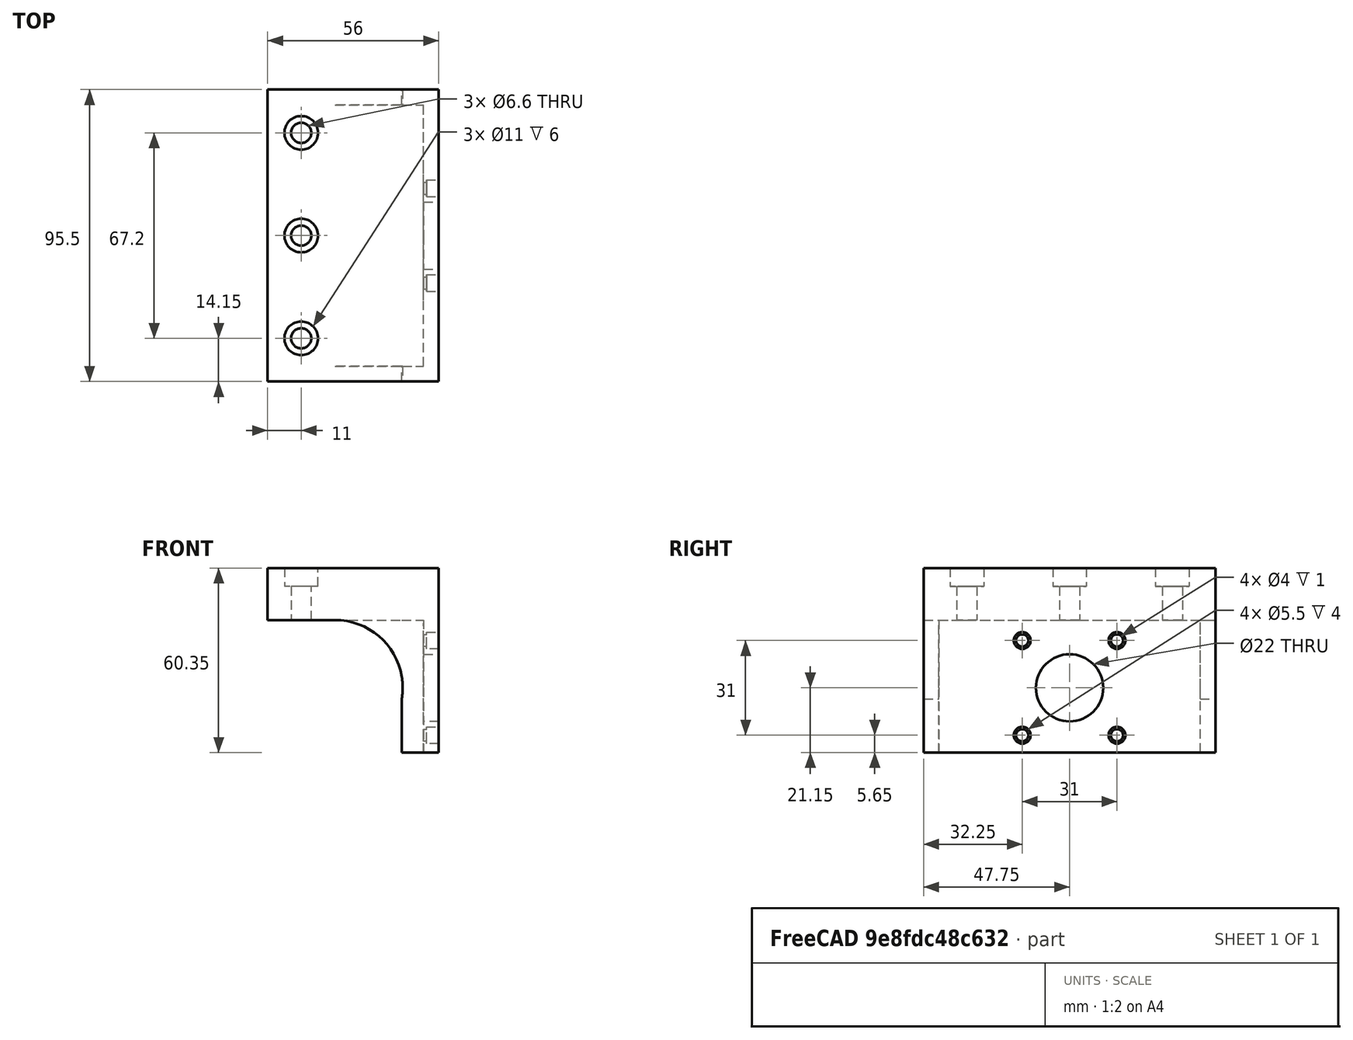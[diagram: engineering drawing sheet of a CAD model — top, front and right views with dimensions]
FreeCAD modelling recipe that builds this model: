
FCSTD DOCUMENT  (FreeCAD 1.0R1.0.0)
Label: CrossTableMount01
License: All rights reserved
LicenseURL: http://en.wikipedia.org/wiki/All_rights_reserved
objects: Part::Cylinder×8, Part::MultiFuse×8, Part::Box×7, Part::Cut×4, Spreadsheet::Sheet×1, Part::Feature×1, Part::Compound×1
note: 29 computed .brp shape members not serialized (recipe doc carries the construction recipe); baked Part::Feature solids carry a one-line shape summary decoded from their .brp

FEATURE [Spreadsheet::Sheet] Spreadsheet
  cells = A2='Slot spacing; B2(slot_spacing)==42.2 - 8.6; E2='Upper thickness; F2(upper_total_thickness)==clamp_screwlen - slot_depth + clamp_headheight; A3='Slot depth; B3(slot_depth)=9; E3='Screw thread thickness; F3(screwhole_len)==clamp_screwlen - slot_depth; A4='Clamp screw through hole; B4(clamp_through)=6.6; C4='M6 medium through hole; A5='Clamp screw length; B5(clamp_screwlen)=20; C5='without head as usual; A6='Clamp screw head diameter; B6(clamp_headdia)=11; C6='Real diameter is 10, want to make sure it fits; A7='Clamp screw head height; B7(clamp_headheight)=6; C7='Real height is 6, want to sink; A8='Tolerance; B8(tolerance)=0.2; A9='Total width; B9(total_width)=95.5; A10='Motor offset horizontal; B10(motor_off_h)=34; A11='Motor offset vertical; B11(motor_off_v)==40 - 18.6 / 2 - 8.5
FEATURE [Part::Box] Box  label="Cube"
  AttacherType = Attacher::AttachEngine3D
  Height = 17
  Length = 56
  Placement = pos=(0,-47.75,0) rot=(0,0,1;0rad)
  Width = 95.5
  expr: .Placement.Base.y = -Spreadsheet.total_width / 2
  expr: Height = <<Spreadsheet>>.upper_total_thickness
  expr: Length = Spreadsheet.clamp_headdia * 2 + Spreadsheet.motor_off_h
  expr: Width = Spreadsheet.total_width
FEATURE [Part::Cylinder] Cylinder
  Angle = 360
  AttacherType = Attacher::AttachEngine3D
  FirstAngle = 0
  Height = 17
  Radius = 3.3
  SecondAngle = 0
  expr: Height = Spreadsheet.upper_total_thickness
  expr: Radius = Spreadsheet.clamp_through / 2
FEATURE [Part::Cylinder] Cylinder001
  Angle = 360
  AttacherType = Attacher::AttachEngine3D
  FirstAngle = 0
  Height = 6
  Placement = pos=(0,0,11) rot=(0,0,1;0rad)
  Radius = 5.5
  SecondAngle = 0
  expr: .Placement.Base.z = Spreadsheet.screwhole_len
  expr: Height = Spreadsheet.clamp_headheight
  expr: Radius = Spreadsheet.clamp_headdia / 2
FEATURE [Part::MultiFuse] Fusion
  Placement = pos=(11,0,0) rot=(0,0,1;0rad)
  Shapes = -> [Cylinder,Cylinder001]
  expr: .Placement.Base.x = Spreadsheet.clamp_headdia
FEATURE [Part::Cylinder] Cylinder002
  Angle = 360
  AttacherType = Attacher::AttachEngine3D
  FirstAngle = 0
  Height = 17
  Radius = 3.3
  SecondAngle = 0
  expr: Height = Spreadsheet.upper_total_thickness
  expr: Radius = Spreadsheet.clamp_through / 2
FEATURE [Part::Cylinder] Cylinder003
  Angle = 360
  AttacherType = Attacher::AttachEngine3D
  FirstAngle = 0
  Height = 6
  Placement = pos=(0,0,11) rot=(0,0,1;0rad)
  Radius = 5.5
  SecondAngle = 0
  expr: .Placement.Base.z = Spreadsheet.screwhole_len
  expr: Height = Spreadsheet.clamp_headheight
  expr: Radius = Spreadsheet.clamp_headdia / 2
FEATURE [Part::MultiFuse] Fusion001
  Placement = pos=(11,33.6,0) rot=(0,0,1;0rad)
  Shapes = -> [Cylinder002,Cylinder003]
  expr: .Placement.Base.x = Spreadsheet.clamp_headdia
  expr: .Placement.Base.y = Spreadsheet.slot_spacing
FEATURE [Part::Cylinder] Cylinder004
  Angle = 360
  AttacherType = Attacher::AttachEngine3D
  FirstAngle = 0
  Height = 17
  Radius = 3.3
  SecondAngle = 0
  expr: Height = Spreadsheet.upper_total_thickness
  expr: Radius = Spreadsheet.clamp_through / 2
FEATURE [Part::Cylinder] Cylinder005
  Angle = 360
  AttacherType = Attacher::AttachEngine3D
  FirstAngle = 0
  Height = 6
  Placement = pos=(0,0,11) rot=(0,0,1;0rad)
  Radius = 5.5
  SecondAngle = 0
  expr: .Placement.Base.z = Spreadsheet.screwhole_len
  expr: Height = Spreadsheet.clamp_headheight
  expr: Radius = Spreadsheet.clamp_headdia / 2
FEATURE [Part::MultiFuse] Fusion002
  Placement = pos=(11,-33.6,0) rot=(0,0,1;0rad)
  Shapes = -> [Cylinder004,Cylinder005]
  expr: .Placement.Base.x = Spreadsheet.clamp_headdia
  expr: .Placement.Base.y = -Spreadsheet.slot_spacing
FEATURE [Part::MultiFuse] Fusion003
  Shapes = -> [Fusion,Fusion001,Fusion002]
FEATURE [Part::Cut] Cut
  Base = -> Box
  Tool = -> Fusion003
FEATURE [Part::Feature] Cut003_solid  label="MountplateTemplate"
  Placement = pos=(0,0,0) rot=(0,1,0;1.5708rad)
  shape: bbox 5 x 42.3 x 42.3 mm, 19 faces (baked)
  expr: .Placement.Base.z = 0
FEATURE [Part::Box] Box001  label="Cube001"
  AttacherType = Attacher::AttachEngine3D
  Height = 60.35
  Length = 5
  Placement = pos=(51,-47.75,-43.35) rot=(0,0,1;0rad)
  Width = 95.5
  expr: .Placement.Base.x = Spreadsheet.motor_off_h - 5 + Spreadsheet.clamp_headdia * 2
  expr: .Placement.Base.y = -Spreadsheet.total_width / 2
  expr: .Placement.Base.z = -(42.3 / 2 + Spreadsheet.motor_off_v)
  expr: Height = 42.3 / 2 + Spreadsheet.motor_off_v + Spreadsheet.upper_total_thickness
  expr: Width = Spreadsheet.total_width
FEATURE [Part::Compound] Compound
  Links = -> [Cut003_solid]
  Placement = pos=(51,0,-22.2) rot=(0,0,1;3.14159rad)
  expr: .Placement.Base.x = Spreadsheet.motor_off_h + Spreadsheet.clamp_headdia * 2 - 5
  expr: .Placement.Base.z = -Spreadsheet.motor_off_v
FEATURE [Part::Box] Box002  label="Cube002"
  AttacherType = Attacher::AttachEngine3D
  Height = 42.3
  Length = 5
  Placement = pos=(51,-21.15,-43.35) rot=(0,0,1;0rad)
  Width = 42.3
  expr: .Placement.Base.x = Spreadsheet.motor_off_h - 5 + Spreadsheet.clamp_headdia * 2
  expr: .Placement.Base.y = -42.3 / 2
  expr: .Placement.Base.z = -Spreadsheet.motor_off_v - 42.3 / 2
FEATURE [Part::Cut] Cut001
  Base = -> Box001
  Tool = -> Box002
FEATURE [Part::MultiFuse] Fusion004
  Shapes = -> [Cut001,Compound]
FEATURE [Part::Box] Box003  label="Cube003"
  AttacherType = Attacher::AttachEngine3D
  Height = 22.2
  Length = 34
  Placement = pos=(22,0,-22.2) rot=(0,0,1;0rad)
  Width = 5
  expr: .Placement.Base.x = Spreadsheet.clamp_headdia * 2
  expr: .Placement.Base.z = -Spreadsheet.motor_off_v
  expr: Height = Spreadsheet.motor_off_v
  expr: Length = Spreadsheet.motor_off_h
FEATURE [Part::Cylinder] Cylinder006
  Angle = 360
  AttacherType = Attacher::AttachEngine3D
  FirstAngle = 0
  Height = 5
  Placement = pos=(22,5,-22.2) rot=(1,0,0;1.5708rad)
  Radius = 22.2
  SecondAngle = 0
  expr: .Placement.Base.x = 2 * Spreadsheet.clamp_headdia
  expr: .Placement.Base.z = -Spreadsheet.motor_off_v
  expr: Radius = Spreadsheet.motor_off_v
FEATURE [Part::Box] Box004  label="Cube004"
  AttacherType = Attacher::AttachEngine3D
  Height = 43.35
  Length = 11.1
  Placement = pos=(43.9,0,-43.35) rot=(0,0,1;0rad)
  Width = 5
  expr: .Placement.Base.x = 2 * Spreadsheet.clamp_headdia + Spreadsheet.motor_off_h - (Spreadsheet.motor_off_h - (Spreadsheet.motor_off_h - Spreadsheet.motor_off_v / 2)) - 1
  expr: .Placement.Base.z = -(Spreadsheet.motor_off_v + 42.3 / 2)
  expr: Height = Spreadsheet.motor_off_v + 42.3 / 2
  expr: Length = Spreadsheet.motor_off_h - (Spreadsheet.motor_off_h - Spreadsheet.motor_off_v / 2)
FEATURE [Part::MultiFuse] Fusion005
  Shapes = -> [Box003,Box004]
FEATURE [Part::Cut] Cut002
  Base = -> Fusion005
  Placement = pos=(0,42.75,0) rot=(0,0,1;0rad)
  Tool = -> Cylinder006
  expr: .Placement.Base.y = Spreadsheet.total_width / 2 - 5
FEATURE [Part::Box] Box005  label="Cube005"
  AttacherType = Attacher::AttachEngine3D
  Height = 22.2
  Length = 34
  Placement = pos=(22,0,-22.2) rot=(0,0,1;0rad)
  Width = 5
  expr: .Placement.Base.x = Spreadsheet.clamp_headdia * 2
  expr: .Placement.Base.z = -Spreadsheet.motor_off_v
  expr: Height = Spreadsheet.motor_off_v
  expr: Length = Spreadsheet.motor_off_h
FEATURE [Part::Box] Box006  label="Cube006"
  AttacherType = Attacher::AttachEngine3D
  Height = 43.35
  Length = 11.1
  Placement = pos=(43.9,0,-43.35) rot=(0,0,1;0rad)
  Width = 5
  expr: .Placement.Base.x = 2 * Spreadsheet.clamp_headdia + Spreadsheet.motor_off_h - (Spreadsheet.motor_off_h - (Spreadsheet.motor_off_h - Spreadsheet.motor_off_v / 2)) - 1
  expr: .Placement.Base.z = -(Spreadsheet.motor_off_v + 42.3 / 2)
  expr: Height = Spreadsheet.motor_off_v + 42.3 / 2
  expr: Length = Spreadsheet.motor_off_h - (Spreadsheet.motor_off_h - Spreadsheet.motor_off_v / 2)
FEATURE [Part::Cylinder] Cylinder007
  Angle = 360
  AttacherType = Attacher::AttachEngine3D
  FirstAngle = 0
  Height = 5
  Placement = pos=(22,5,-22.2) rot=(1,0,0;1.5708rad)
  Radius = 22.2
  SecondAngle = 0
  expr: .Placement.Base.x = 2 * Spreadsheet.clamp_headdia
  expr: .Placement.Base.z = -Spreadsheet.motor_off_v
  expr: Radius = Spreadsheet.motor_off_v
FEATURE [Part::MultiFuse] Fusion006
  Shapes = -> [Box005,Box006]
FEATURE [Part::Cut] Cut003
  Base = -> Fusion006
  Placement = pos=(0,-47.75,0) rot=(0,0,1;0rad)
  Tool = -> Cylinder007
  expr: .Placement.Base.y = -Spreadsheet.total_width / 2
FEATURE [Part::MultiFuse] Fusion007
  Shapes = -> [Cut003,Cut,Fusion004,Cut002]
